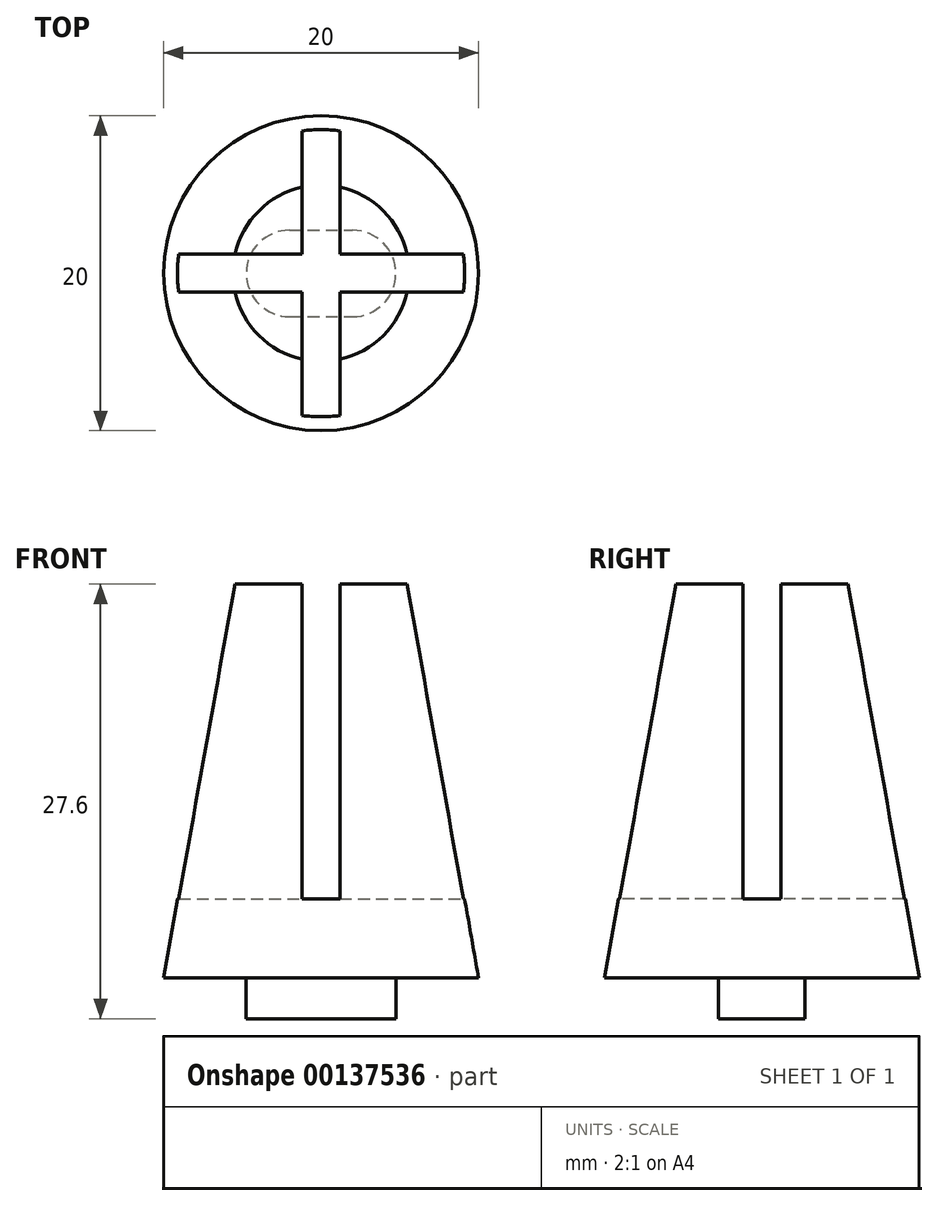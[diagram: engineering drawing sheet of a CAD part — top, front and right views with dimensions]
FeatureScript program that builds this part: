
annotation { "Feature Type Name" : "Feature", "Feature Type Description" : "" }
export const myFeature = defineFeature(function(context is Context, id is Id, definition is map)
    precondition{}
    {
        {
            var Q0;
            Q0=qCreatedBy(makeId("Top.planeOp"),FACE);
            var sketch = newSketch(context, id + "F0", { "sketchPlane" : qUnion([Q0])});
            skCircle(sketch, "E0", {"center": v(0, 0) * mm, "radius": 10 * mm});
            skSolve(sketch);
        }
        {
            var Q0;
            Q0=makeQuery(id+"F0.imprint","IMPRINT",FACE,{"disambiguationData":[TD([[makeQuery(id+"F0.imprint","IMPRINT",EDGE,{"derivedFrom":sQuery(id+"F0.wireOp",EDGE,"E0")}),1.0]])]});
            extrude(context, id + "F1", {"entities" : qUnion([Q0]), "depth" : 30 * mm, "hasDraft" : true, "draftAngle" : 10 * degree, "draftPullDirection" : true});
        }
        {
            var Q0;
            Q0=makeQuery(id+"F1.opExtrude","CAP_FACE",FACE,{"disambiguationData":[OSD([sQuery(id+"F0.wireOp",EDGE,"E0")])],"isStart":false});
            var sketch = newSketch(context, id + "F2", { "sketchPlane" : qUnion([Q0])});
            skLineSegment(sketch, "E1.bottom", {"start": v(-1.2, 21.92) * mm, "end": v(1.2, 21.92) * mm});
            skLineSegment(sketch, "E1.top", {"start": v(-1.2, -22.11) * mm, "end": v(1.2, -22.11) * mm});
            skLineSegment(sketch, "E1.left", {"start": v(-1.2, 21.92) * mm, "end": v(-1.2, -22.11) * mm});
            skLineSegment(sketch, "E1.right", {"start": v(1.2, 21.92) * mm, "end": v(1.2, -22.11) * mm});
            skLineSegment(sketch, "E2.bottom", {"start": v(-22.63, 1.2) * mm, "end": v(23.26, 1.2) * mm});
            skLineSegment(sketch, "E2.top", {"start": v(-22.63, -1.2) * mm, "end": v(23.26, -1.2) * mm});
            skLineSegment(sketch, "E2.left", {"start": v(-22.63, 1.2) * mm, "end": v(-22.63, -1.2) * mm});
            skLineSegment(sketch, "E2.right", {"start": v(23.26, 1.2) * mm, "end": v(23.26, -1.2) * mm});
            skSolve(sketch);
        }
        {
            var Q0;
            Q0 = qSketchRegion(id + "F2", true);
            extrude(context, id + "F3", {"entities" : qUnion([Q0]), "operationType" : NewBodyOperationType.REMOVE, "oppositeDirection" : true, "depth" : 25 * mm});
        }
        {
            var Q0;
            Q0=makeQuery(id+"F1.opExtrude","CAP_FACE",FACE,{"disambiguationData":[OSD([sQuery(id+"F0.wireOp",EDGE,"E0")])],"isStart":true});
            var sketch = newSketch(context, id + "F4", { "sketchPlane" : qUnion([Q0])});
            skLineSegment(sketch, "E3", {"start": v(-2, 2.76) * mm, "end": v(2, 2.76) * mm});
            skLineSegment(sketch, "E4", {"start": v(-2, -2.74) * mm, "end": v(2, -2.74) * mm});
            skArc(sketch, "E5", {"start": v(2, -2.74) * mm, "mid": v(4.75, 0.01) * mm, "end": v(2, 2.76) * mm});
            skArc(sketch, "E6", {"start": v(-2, 2.76) * mm, "mid": v(-4.75, 0.01) * mm, "end": v(-2, -2.74) * mm});
            skSolve(sketch);
        }
        {
            var Q0;
            Q0=makeQuery(id+"F4.imprint","IMPRINT",FACE,{"disambiguationData":[TD([[makeQuery(id+"F4.imprint","IMPRINT",EDGE,{"derivedFrom":sQuery(id+"F4.wireOp",EDGE,"E3")}),-1.0]])]});
            var Q1;
            Q1=makeQuery(id+"F3.boolean.opBoolean","COPY",FACE,{"derivedFrom":makeQuery(id+"F3.opExtrude","CAP_FACE",FACE,{"disambiguationData":[OSD([sQuery(id+"F2.wireOp",EDGE,"E1.bottom"),sQuery(id+"F2.wireOp",EDGE,"E1.top"),sQuery(id+"F2.wireOp",EDGE,"E1.left"),sQuery(id+"F2.wireOp",EDGE,"E1.right"),sQuery(id+"F2.wireOp",EDGE,"E2.bottom"),sQuery(id+"F2.wireOp",EDGE,"E2.top"),sQuery(id+"F2.wireOp",EDGE,"E2.left"),sQuery(id+"F2.wireOp",EDGE,"E2.right")])],"isStart":false})});
            extrude(context, id + "F5", {"entities" : qUnion([Q0]), "operationType" : NewBodyOperationType.ADD, "endBoundEntityFace" : qUnion([Q1]), "depth" : 2.6 * mm});
        }
        {
            var Q0;
            Q0=qCreatedBy(makeId("Front.planeOp"),FACE);
            var sketch = newSketch(context, id + "F6", { "sketchPlane" : qUnion([Q0])});
            skLineSegment(sketch, "E7", {"start": v(-10, 0) * mm, "end": v(-9.12, 5) * mm});
            skLineSegment(sketch, "E8", {"start": v(9.12, 5) * mm, "end": v(10, 0) * mm});
            skLineSegment(sketch, "E9.0", {"start": v(-4.55, 30) * mm, "end": v(-1.2, 30) * mm});
            skLineSegment(sketch, "E10.0", {"start": v(1.2, 30) * mm, "end": v(4.55, 30) * mm});
            skLineSegment(sketch, "E11.bottom", {"start": v(-12.88, 30) * mm, "end": v(13.3, 30) * mm});
            skLineSegment(sketch, "E11.top", {"start": v(-12.88, 25) * mm, "end": v(13.3, 25) * mm});
            skLineSegment(sketch, "E11.left", {"start": v(-12.88, 30) * mm, "end": v(-12.88, 25) * mm});
            skLineSegment(sketch, "E11.right", {"start": v(13.3, 30) * mm, "end": v(13.3, 25) * mm});
            skSolve(sketch);
        }
        {
            var Q0;
            Q0=makeQuery(id+"F6.imprint","IMPRINT",FACE,{"disambiguationData":[TD([[makeQuery(id+"F6.imprint","IMPRINT",EDGE,{"derivedFrom":sQuery(id+"F6.wireOp",EDGE,"E11.top")}),1.0]])]});
            extrude(context, id + "F7", {"entities" : qUnion([Q0]), "operationType" : NewBodyOperationType.REMOVE, "depth" : 25 * mm, "hasSecondDirection" : true, "secondDirectionOppositeDirection" : true, "secondDirectionDepth" : 25 * mm});
        }
    });
